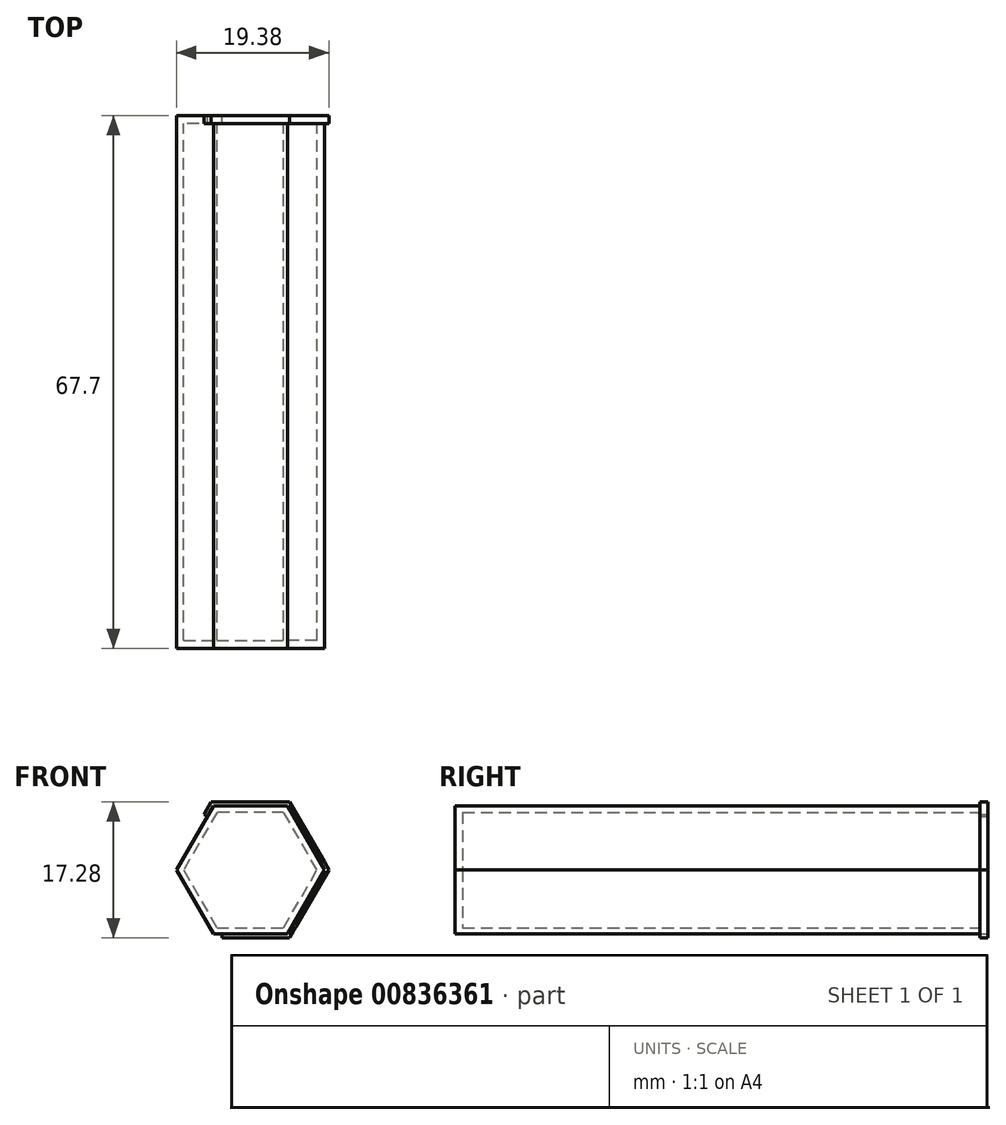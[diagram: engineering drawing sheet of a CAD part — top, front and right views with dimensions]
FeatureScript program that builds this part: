
annotation { "Feature Type Name" : "Feature", "Feature Type Description" : "" }
export const myFeature = defineFeature(function(context is Context, id is Id, definition is map)
    precondition{}
    {
        {
            var Q0;
            Q0=qCreatedBy(makeId("Front.planeOp"),FACE);
            var sketch = newSketch(context, id + "F0", { "sketchPlane" : qUnion([Q0])});
            skLineSegment(sketch, "E0.0", {"start": v(9.4, 0) * mm, "end": v(4.7, -8.14) * mm});
            skLineSegment(sketch, "E0.1", {"start": v(4.7, -8.14) * mm, "end": v(-4.7, -8.14) * mm});
            skLineSegment(sketch, "E0.2", {"start": v(-4.7, -8.14) * mm, "end": v(-9.4, 0) * mm});
            skLineSegment(sketch, "E0.3", {"start": v(-9.4, 0) * mm, "end": v(-4.7, 8.14) * mm});
            skLineSegment(sketch, "E0.4", {"start": v(-4.7, 8.14) * mm, "end": v(4.7, 8.14) * mm});
            skLineSegment(sketch, "E0.5", {"start": v(4.7, 8.14) * mm, "end": v(9.4, 0) * mm});
            skSolve(sketch);
        }
        {
            var Q0;
            Q0=makeQuery(id+"F0.imprint","IMPRINT",FACE,{"disambiguationData":[TD([[makeQuery(id+"F0.imprint","IMPRINT",EDGE,{"derivedFrom":sQuery(id+"F0.wireOp",EDGE,"E0.0")}),-1.0]])]});
            extrude(context, id + "F1", {"entities" : qUnion([Q0]), "depth" : 68.5 * mm, "offsetDistance" : 25 * mm});
        }
        {
            var Q0;
            Q0=makeQuery(id+"F1.opExtrude","CAP_FACE",FACE,{"disambiguationData":[OSD([sQuery(id+"F0.wireOp",EDGE,"E0.0"),sQuery(id+"F0.wireOp",EDGE,"E0.1"),sQuery(id+"F0.wireOp",EDGE,"E0.2"),sQuery(id+"F0.wireOp",EDGE,"E0.3"),sQuery(id+"F0.wireOp",EDGE,"E0.4"),sQuery(id+"F0.wireOp",EDGE,"E0.5")])],"isStart":true});
            shell(context, id + "F2", {"entities" : qUnion([Q0]), "thickness" : 0.8 * mm});
        }
        {
            var Q0;
            Q0=makeQuery(id+"F1.opExtrude","CAP_FACE",FACE,{"disambiguationData":[OSD([sQuery(id+"F0.wireOp",EDGE,"E0.0"),sQuery(id+"F0.wireOp",EDGE,"E0.1"),sQuery(id+"F0.wireOp",EDGE,"E0.2"),sQuery(id+"F0.wireOp",EDGE,"E0.3"),sQuery(id+"F0.wireOp",EDGE,"E0.4"),sQuery(id+"F0.wireOp",EDGE,"E0.5")])],"isStart":false});
            extrude(context, id + "F3", {"entities" : qUnion([Q0]), "operationType" : NewBodyOperationType.REMOVE, "oppositeDirection" : true, "depth" : 0.8 * mm, "offsetDistance" : 25 * mm});
        }
        {
            var Q0;
            Q0=makeQuery(id+"F3.boolean.opBoolean","COPY",FACE,{"derivedFrom":makeQuery(id+"F3.opExtrude","CAP_FACE",FACE,{"disambiguationData":[OSD([sQuery(id+"F0.wireOp",EDGE,"E0.0"),sQuery(id+"F0.wireOp",EDGE,"E0.1"),sQuery(id+"F0.wireOp",EDGE,"E0.2"),sQuery(id+"F0.wireOp",EDGE,"E0.3"),sQuery(id+"F0.wireOp",EDGE,"E0.4"),sQuery(id+"F0.wireOp",EDGE,"E0.5")])],"isStart":false})});
            var sketch = newSketch(context, id + "F4", { "sketchPlane" : qUnion([Q0])});
            skLineSegment(sketch, "E1", {"start": v(4.24, 7.34) * mm, "end": v(8.48, 0) * mm});
            skLineSegment(sketch, "E2", {"start": v(9.4, 0) * mm, "end": v(4.7, 8.14) * mm});
            skLineSegment(sketch, "E3", {"start": v(-8.48, 0) * mm, "end": v(-4.24, -7.34) * mm});
            skLineSegment(sketch, "E4", {"start": v(-9.4, 0) * mm, "end": v(-4.7, -8.14) * mm});
            skLineSegment(sketch, "E5", {"start": v(4.7, 8.14) * mm, "end": v(7.05, 4.07) * mm});
            skLineSegment(sketch, "E6", {"start": v(7.05, 4.07) * mm, "end": v(-7.05, -4.07) * mm});
            skLineSegment(sketch, "E7", {"start": v(-4.7, -8.14) * mm, "end": v(-7.05, -4.07) * mm});
            skLineSegment(sketch, "E8", {"start": v(6.36, 3.67) * mm, "end": v(-6.36, -3.67) * mm});
            skSolve(sketch);
        }
        {
            var Q0;
            {var subQ3=sQuery(id+"F4.wireOp",EDGE,"E8");Q0=makeQuery(id+"F4.imprint","IMPRINT",FACE,{"disambiguationData":[TD([[makeQuery(id+"F4.imprint","IMPRINT",EDGE,{"derivedFrom":subQ3}),-1.0]])]});}
            var sketch = newSketch(context, id + "F5", { "sketchPlane" : qUnion([Q0])});
            skLineSegment(sketch, "E9", {"start": v(-4.24, 7.34) * mm, "end": v(4.24, 7.34) * mm});
            skLineSegment(sketch, "E10", {"start": v(4.24, 7.34) * mm, "end": v(8.48, 0) * mm});
            skLineSegment(sketch, "E11", {"start": v(8.48, 0) * mm, "end": v(4.24, -7.34) * mm});
            skLineSegment(sketch, "E12", {"start": v(4.24, -7.34) * mm, "end": v(-4.24, -7.34) * mm});
            skLineSegment(sketch, "E13", {"start": v(-4.24, -7.34) * mm, "end": v(-8.48, 0) * mm});
            skLineSegment(sketch, "E14", {"start": v(-8.48, 0) * mm, "end": v(-4.24, 7.34) * mm});
            skLineSegment(sketch, "E15", {"start": v(-3.58, 7.34) * mm, "end": v(-3.58, 6.84) * mm});
            skLineSegment(sketch, "E16", {"start": v(4.7, 6.53) * mm, "end": v(4.27, 6.28) * mm});
            skLineSegment(sketch, "E17", {"start": v(7.83, 1.12) * mm, "end": v(7.4, 0.87) * mm});
            skLineSegment(sketch, "E18", {"start": v(7.83, -1.12) * mm, "end": v(7.4, -0.87) * mm});
            skLineSegment(sketch, "E19", {"start": v(5, -6.03) * mm, "end": v(4.56, -5.78) * mm});
            skLineSegment(sketch, "E20", {"start": v(3.25, -7.34) * mm, "end": v(3.25, -6.84) * mm});
            skLineSegment(sketch, "E21", {"start": v(-3.25, -7.34) * mm, "end": v(-3.25, -6.84) * mm});
            skLineSegment(sketch, "E22", {"start": v(-4.97, -6.08) * mm, "end": v(-4.54, -5.83) * mm});
            skLineSegment(sketch, "E23", {"start": v(-7.63, -1.46) * mm, "end": v(-7.2, -1.21) * mm});
            skLineSegment(sketch, "E24", {"start": v(-7.87, 1.05) * mm, "end": v(-7.44, 0.8) * mm});
            skLineSegment(sketch, "E25", {"start": v(-5.05, 5.93) * mm, "end": v(-4.62, 5.68) * mm});
            skLineSegment(sketch, "E26", {"start": v(3.83, 7.34) * mm, "end": v(3.83, 6.84) * mm});
            skLineSegment(sketch, "E27", {"start": v(-3.58, 6.84) * mm, "end": v(4.17, 6.84) * mm});
            skLineSegment(sketch, "E28", {"start": v(4.27, 6.28) * mm, "end": v(8.04, -0.24) * mm});
            skLineSegment(sketch, "E29", {"start": v(7.4, -0.87) * mm, "end": v(3.81, -7.07) * mm});
            skLineSegment(sketch, "E30", {"start": v(3.25, -6.84) * mm, "end": v(-4.11, -6.84) * mm});
            skLineSegment(sketch, "E31", {"start": v(-4.54, -5.83) * mm, "end": v(-8.02, 0.2) * mm});
            skLineSegment(sketch, "E32", {"start": v(-7.44, 0.8) * mm, "end": v(-3.95, 6.84) * mm});
            skLineSegment(sketch, "E33", {"start": v(-3.95, 6.84) * mm, "end": v(-3.58, 6.84) * mm});
            skLineSegment(sketch, "E34", {"start": v(4.27, 6.28) * mm, "end": v(3.95, 6.84) * mm});
            skLineSegment(sketch, "E35", {"start": v(7.4, -0.87) * mm, "end": v(7.9, 0) * mm});
            skLineSegment(sketch, "E36", {"start": v(3.25, -6.84) * mm, "end": v(3.95, -6.84) * mm});
            skLineSegment(sketch, "E37", {"start": v(-4.54, -5.83) * mm, "end": v(-3.95, -6.84) * mm});
            skLineSegment(sketch, "E38", {"start": v(-7.44, 0.8) * mm, "end": v(-7.9, 0) * mm});
            skSolve(sketch);
        }
        {
            var Q0;
            Q0=qSketchRegion(id+"F5",true);
            extrude(context, id + "F6", {"entities" : qUnion([Q0]), "operationType" : NewBodyOperationType.ADD, "oppositeDirection" : true, "depth" : 1 * mm, "offsetDistance" : 25 * mm});
        }
        {
            var Q0;
            Q0=makeQuery(id+"F1.opExtrude","CAP_FACE",FACE,{"disambiguationData":[OSD([sQuery(id+"F0.wireOp",EDGE,"E0.0"),sQuery(id+"F0.wireOp",EDGE,"E0.1"),sQuery(id+"F0.wireOp",EDGE,"E0.2"),sQuery(id+"F0.wireOp",EDGE,"E0.3"),sQuery(id+"F0.wireOp",EDGE,"E0.4"),sQuery(id+"F0.wireOp",EDGE,"E0.5")])],"isStart":true});
            var sketch = newSketch(context, id + "F7", { "sketchPlane" : qUnion([Q0])});
            skLineSegment(sketch, "E39.0", {"start": v(4.7, 8.14) * mm, "end": v(9.4, 0) * mm});
            skLineSegment(sketch, "E39.1", {"start": v(9.4, 0) * mm, "end": v(4.7, -8.14) * mm});
            skLineSegment(sketch, "E39.2", {"start": v(4.7, -8.14) * mm, "end": v(-4.7, -8.14) * mm});
            skLineSegment(sketch, "E39.3", {"start": v(-4.7, -8.14) * mm, "end": v(-9.4, 0) * mm});
            skLineSegment(sketch, "E39.4", {"start": v(-9.4, 0) * mm, "end": v(-4.7, 8.14) * mm});
            skLineSegment(sketch, "E39.5", {"start": v(-4.7, 8.14) * mm, "end": v(4.7, 8.14) * mm});
            skPoint(sketch, "E39.0.midPoint", {"position": v(7.05, 4.07) * mm});
            skLineSegment(sketch, "E40", {"start": v(-3.98, 8.14) * mm, "end": v(-3.98, 8.64) * mm});
            skLineSegment(sketch, "E41", {"start": v(4, 8.14) * mm, "end": v(4, 8.64) * mm});
            skLineSegment(sketch, "E42", {"start": v(5.45, 6.83) * mm, "end": v(5.89, 7.08) * mm});
            skLineSegment(sketch, "E43", {"start": v(8.73, 1.16) * mm, "end": v(9.16, 1.41) * mm});
            skLineSegment(sketch, "E44", {"start": v(8.94, -0.8) * mm, "end": v(9.37, -1.06) * mm});
            skLineSegment(sketch, "E45", {"start": v(5.6, -6.57) * mm, "end": v(6.04, -6.82) * mm});
            skLineSegment(sketch, "E46", {"start": v(3.6, -8.14) * mm, "end": v(3.6, -8.64) * mm});
            skLineSegment(sketch, "E47", {"start": v(-3.29, -8.14) * mm, "end": v(-3.29, -8.64) * mm});
            skLineSegment(sketch, "E48", {"start": v(-5.4, -6.93) * mm, "end": v(-5.83, -7.18) * mm});
            skLineSegment(sketch, "E49", {"start": v(-8.64, -1.3) * mm, "end": v(-9.08, -1.56) * mm});
            skLineSegment(sketch, "E50", {"start": v(-8.97, 0.75) * mm, "end": v(-9.4, 1) * mm});
            skLineSegment(sketch, "E51", {"start": v(-5.16, 7.35) * mm, "end": v(-5.6, 7.6) * mm});
            skLineSegment(sketch, "E52", {"start": v(-3.98, 8.64) * mm, "end": v(6.07, 8.64) * mm});
            skLineSegment(sketch, "E53", {"start": v(5.89, 7.08) * mm, "end": v(10.3, -0.54) * mm});
            skLineSegment(sketch, "E54", {"start": v(9.37, -1.06) * mm, "end": v(4.8, -8.98) * mm});
            skLineSegment(sketch, "E55", {"start": v(3.6, -8.64) * mm, "end": v(4.99, -8.64) * mm});
            skLineSegment(sketch, "E56", {"start": v(3.6, -8.64) * mm, "end": v(-6.12, -8.64) * mm});
            skLineSegment(sketch, "E57", {"start": v(-5.83, -7.18) * mm, "end": v(-4.99, -8.64) * mm});
            skLineSegment(sketch, "E58", {"start": v(-5.83, -7.18) * mm, "end": v(-10.5, 0.9) * mm});
            skLineSegment(sketch, "E59", {"start": v(-9.4, 1) * mm, "end": v(-9.98, 0) * mm});
            skLineSegment(sketch, "E60", {"start": v(-9.4, 1) * mm, "end": v(-4.76, 9.03) * mm});
            skLineSegment(sketch, "E61", {"start": v(-3.98, 8.64) * mm, "end": v(-4.99, 8.64) * mm});
            skLineSegment(sketch, "E62", {"start": v(5.89, 7.08) * mm, "end": v(4.99, 8.64) * mm});
            skLineSegment(sketch, "E63", {"start": v(9.37, -1.06) * mm, "end": v(9.98, 0) * mm});
            skSolve(sketch);
        }
        {
            var Q0;
            Q0=qSketchRegion(id+"F7",true);
            extrude(context, id + "F8", {"entities" : qUnion([Q0]), "operationType" : NewBodyOperationType.ADD, "oppositeDirection" : true, "depth" : 1 * mm, "offsetDistance" : 25 * mm});
        }
    });
